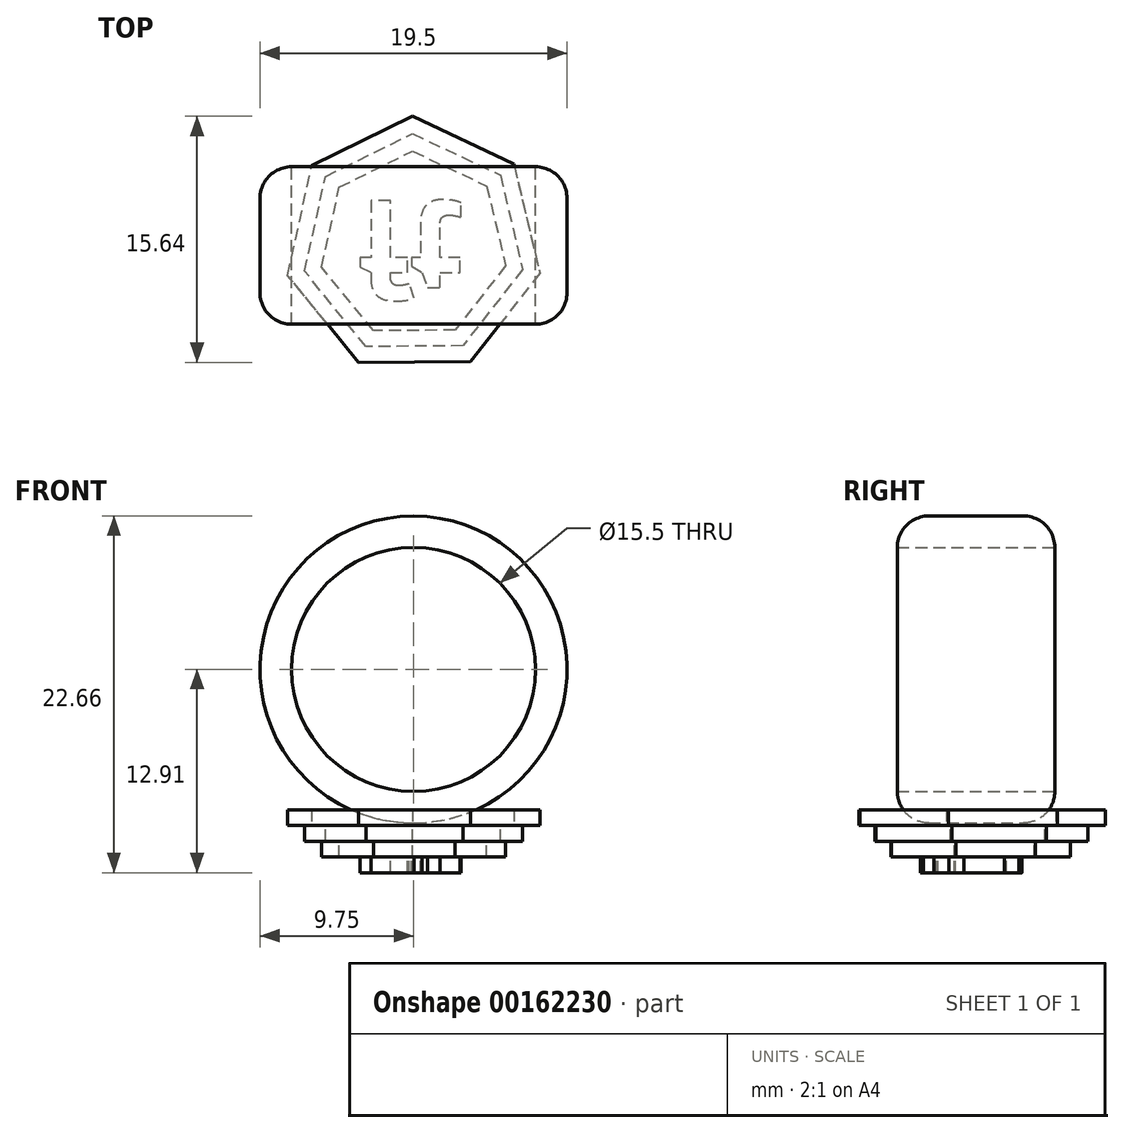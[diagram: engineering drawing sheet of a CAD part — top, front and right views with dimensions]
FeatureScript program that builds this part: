
annotation { "Feature Type Name" : "Feature", "Feature Type Description" : "" }
export const myFeature = defineFeature(function(context is Context, id is Id, definition is map)
    precondition{}
    {
        {
            var Q0;
            Q0=qCreatedBy(makeId("Front.planeOp"),FACE);
            var sketch = newSketch(context, id + "F0", { "sketchPlane" : qUnion([Q0])});
            skCircle(sketch, "E0", {"center": v(0, 9.91) * mm, "radius": 7.75 * mm});
            skCircle(sketch, "E1.0", {"center": v(0, 9.91) * mm, "radius": 9.75 * mm});
            skSolve(sketch);
        }
        {
            var Q0;
            Q0=makeQuery(id+"F0.imprint","IMPRINT",FACE,{"disambiguationData":[TD([[makeQuery(id+"F0.imprint","IMPRINT",EDGE,{"derivedFrom":sQuery(id+"F0.wireOp",EDGE,"E0")}),-1.0]])]});
            extrude(context, id + "F1", {"entities" : qUnion([Q0]), "endBound" : BoundingType.SYMMETRIC, "depth" : 10 * mm});
        }
        {
            var Q0;
            Q0=makeQuery(id+"F1.opExtrude","CAP_EDGE",EDGE,{"disambiguationData":[OSD([sQuery(id+"F0.wireOp",EDGE,"E1.0")])],"isStart":false});
            var Q1;
            Q1=makeQuery(id+"F1.opExtrude","CAP_EDGE",EDGE,{"disambiguationData":[OSD([sQuery(id+"F0.wireOp",EDGE,"E1.0")])],"isStart":true});
            fillet(context, id + "F2", {"entities" : qUnion([Q0, Q1]), "radius" : 2 * mm, "tangentPropagation" : true, "allowEdgeOverflow" : false});
        }
        {
            var Q0;
            Q0=qCreatedBy(makeId("Top.planeOp"),FACE);
            var sketch = newSketch(context, id + "F3", { "sketchPlane" : qUnion([Q0])});
            skCircle(sketch, "E2.cCircle", {"center": v(0, 0) * mm, "radius": 7.4 * mm, "construction": true});
            skLineSegment(sketch, "E2.0", {"start": v(6.37, 5.17) * mm, "end": v(8.02, -1.76) * mm});
            skLineSegment(sketch, "E2.1", {"start": v(8.02, -1.76) * mm, "end": v(3.63, -7.37) * mm});
            skLineSegment(sketch, "E2.2", {"start": v(3.63, -7.37) * mm, "end": v(-3.5, -7.43) * mm});
            skLineSegment(sketch, "E2.3", {"start": v(-3.5, -7.43) * mm, "end": v(-7.99, -1.9) * mm});
            skLineSegment(sketch, "E2.4", {"start": v(-7.99, -1.9) * mm, "end": v(-6.46, 5.06) * mm});
            skLineSegment(sketch, "E2.5", {"start": v(-6.46, 5.06) * mm, "end": v(-0.07, 8.2) * mm});
            skLineSegment(sketch, "E2.6", {"start": v(-0.07, 8.2) * mm, "end": v(6.37, 5.17) * mm});
            skPoint(sketch, "E2.0.midPoint", {"position": v(7.2, 1.7) * mm});
            skSolve(sketch);
        }
        {
            var Q0;
            Q0=makeQuery(id+"F3.imprint","IMPRINT",FACE,{"disambiguationData":[TD([[makeQuery(id+"F3.imprint","IMPRINT",EDGE,{"derivedFrom":sQuery(id+"F3.wireOp",EDGE,"E2.0")}),-1.0]])]});
            extrude(context, id + "F4", {"entities" : qUnion([Q0]), "depth" : 1 * mm});
        }
        {
            var Q0;
            Q0=makeQuery(id+"F4.opExtrude","CAP_FACE",FACE,{"disambiguationData":[OSD([sQuery(id+"F3.wireOp",EDGE,"E2.0"),sQuery(id+"F3.wireOp",EDGE,"E2.1"),sQuery(id+"F3.wireOp",EDGE,"E2.2"),sQuery(id+"F3.wireOp",EDGE,"E2.3"),sQuery(id+"F3.wireOp",EDGE,"E2.4"),sQuery(id+"F3.wireOp",EDGE,"E2.5"),sQuery(id+"F3.wireOp",EDGE,"E2.6")])],"isStart":true});
            var sketch = newSketch(context, id + "F5", { "sketchPlane" : qUnion([Q0])});
            skLineSegment(sketch, "E3.0", {"start": v(3.63, 7.37) * mm, "end": v(-3.5, 7.43) * mm});
            skLineSegment(sketch, "E4.0.0", {"start": v(6.37, -5.17) * mm, "end": v(8.02, 1.76) * mm});
            skLineSegment(sketch, "E4.0.1", {"start": v(8.02, 1.76) * mm, "end": v(3.63, 7.37) * mm});
            skLineSegment(sketch, "E4.0.3", {"start": v(-3.5, 7.43) * mm, "end": v(-7.99, 1.9) * mm});
            skLineSegment(sketch, "E4.0.4", {"start": v(-7.99, 1.9) * mm, "end": v(-6.46, -5.06) * mm});
            skLineSegment(sketch, "E4.0.5", {"start": v(-6.46, -5.06) * mm, "end": v(-0.07, -8.2) * mm});
            skLineSegment(sketch, "E4.0.6", {"start": v(-0.07, -8.2) * mm, "end": v(6.37, -5.17) * mm});
            skLineSegment(sketch, "E5.0", {"start": v(-0.06, -7.1) * mm, "end": v(5.51, -4.47) * mm});
            skLineSegment(sketch, "E5.1", {"start": v(-5.59, -4.38) * mm, "end": v(-0.06, -7.1) * mm});
            skLineSegment(sketch, "E5.2", {"start": v(6.94, 1.52) * mm, "end": v(3.14, 6.37) * mm});
            skLineSegment(sketch, "E5.3", {"start": v(3.14, 6.37) * mm, "end": v(-3.03, 6.42) * mm});
            skLineSegment(sketch, "E5.4", {"start": v(-3.03, 6.42) * mm, "end": v(-6.9, 1.64) * mm});
            skLineSegment(sketch, "E5.5", {"start": v(5.51, -4.47) * mm, "end": v(6.94, 1.52) * mm});
            skLineSegment(sketch, "E5.6", {"start": v(-6.9, 1.64) * mm, "end": v(-5.59, -4.38) * mm});
            skSolve(sketch);
        }
        {
            var Q0;
            Q0=makeQuery(id+"F5.imprint","IMPRINT",FACE,{"disambiguationData":[TD([[makeQuery(id+"F5.imprint","IMPRINT",EDGE,{"derivedFrom":sQuery(id+"F5.wireOp",EDGE,"E5.0")}),1.0]])]});
            extrude(context, id + "F6", {"entities" : qUnion([Q0]), "depth" : 1 * mm});
        }
        {
            var Q0;
            Q0=makeQuery(id+"F6.opExtrude","CAP_FACE",FACE,{"disambiguationData":[OSD([sQuery(id+"F5.wireOp",EDGE,"E5.0"),sQuery(id+"F5.wireOp",EDGE,"E5.1"),sQuery(id+"F5.wireOp",EDGE,"E5.2"),sQuery(id+"F5.wireOp",EDGE,"E5.3"),sQuery(id+"F5.wireOp",EDGE,"E5.4"),sQuery(id+"F5.wireOp",EDGE,"E5.5"),sQuery(id+"F5.wireOp",EDGE,"E5.6")])],"isStart":false});
            var sketch = newSketch(context, id + "F7", { "sketchPlane" : qUnion([Q0])});
            skLineSegment(sketch, "E6.0.0", {"start": v(-5.59, -4.38) * mm, "end": v(-0.06, -7.1) * mm});
            skLineSegment(sketch, "E6.0.1", {"start": v(-0.06, -7.1) * mm, "end": v(5.51, -4.47) * mm});
            skLineSegment(sketch, "E6.0.2", {"start": v(5.51, -4.47) * mm, "end": v(6.94, 1.52) * mm});
            skLineSegment(sketch, "E6.0.3", {"start": v(6.94, 1.52) * mm, "end": v(3.14, 6.37) * mm});
            skLineSegment(sketch, "E6.0.4", {"start": v(3.14, 6.37) * mm, "end": v(-3.03, 6.42) * mm});
            skLineSegment(sketch, "E6.0.5", {"start": v(-3.03, 6.42) * mm, "end": v(-6.9, 1.64) * mm});
            skLineSegment(sketch, "E6.0.6", {"start": v(-6.9, 1.64) * mm, "end": v(-5.59, -4.38) * mm});
            skLineSegment(sketch, "E7.0", {"start": v(-5.83, 1.38) * mm, "end": v(-4.72, -3.7) * mm});
            skLineSegment(sketch, "E7.1", {"start": v(-2.55, 5.42) * mm, "end": v(-5.83, 1.38) * mm});
            skLineSegment(sketch, "E7.2", {"start": v(-0.05, -5.99) * mm, "end": v(4.65, -3.78) * mm});
            skLineSegment(sketch, "E7.3", {"start": v(4.65, -3.78) * mm, "end": v(5.85, 1.28) * mm});
            skLineSegment(sketch, "E7.4", {"start": v(5.85, 1.28) * mm, "end": v(2.65, 5.37) * mm});
            skLineSegment(sketch, "E7.5", {"start": v(-4.72, -3.7) * mm, "end": v(-0.05, -5.99) * mm});
            skLineSegment(sketch, "E7.6", {"start": v(2.65, 5.37) * mm, "end": v(-2.55, 5.42) * mm});
            skSolve(sketch);
        }
        {
            var Q0;
            Q0=makeQuery(id+"F7.imprint","IMPRINT",FACE,{"disambiguationData":[TD([[makeQuery(id+"F7.imprint","IMPRINT",EDGE,{"derivedFrom":sQuery(id+"F7.wireOp",EDGE,"E7.0")}),1.0]])]});
            extrude(context, id + "F8", {"entities" : qUnion([Q0]), "depth" : 1 * mm});
        }
        {
            var Q0;
            Q0=makeQuery(id+"F8.opExtrude","CAP_FACE",FACE,{"disambiguationData":[OSD([sQuery(id+"F7.wireOp",EDGE,"E7.0"),sQuery(id+"F7.wireOp",EDGE,"E7.1"),sQuery(id+"F7.wireOp",EDGE,"E7.2"),sQuery(id+"F7.wireOp",EDGE,"E7.3"),sQuery(id+"F7.wireOp",EDGE,"E7.4"),sQuery(id+"F7.wireOp",EDGE,"E7.5"),sQuery(id+"F7.wireOp",EDGE,"E7.6")])],"isStart":false});
            var sketch = newSketch(context, id + "F9", { "sketchPlane" : qUnion([Q0])});
            skText(sketch, "E8", { "text": "ft", "fontName": "OpenSans-Bold.ttf"});
            const initialGuessF9  = {"E8": [-0.00356, -0.00284, 1, 0, 0.006]};
            skSetInitialGuess(sketch, initialGuessF9);
            skSolve(sketch);
        }
        {
            var Q0;
            Q0=makeQuery(id+"F9.imprint","IMPRINT",FACE,{"disambiguationData":[TD([[makeQuery(id+"F9.imprint","IMPRINT",EDGE,{"derivedFrom":sQuery(id+"F9.wireOp",EDGE,"E8.sketch_text.stroke-0")}),-1.0]])]});
            var Q1;
            Q1=makeQuery(id+"F9.imprint","IMPRINT",FACE,{"disambiguationData":[TD([[makeQuery(id+"F9.imprint","IMPRINT",EDGE,{"derivedFrom":sQuery(id+"F9.wireOp",EDGE,"E8.sketch_text.stroke-18")}),-1.0]])]});
            extrude(context, id + "F10", {"entities" : qUnion([Q0, Q1]), "depth" : 1 * mm});
        }
    });
